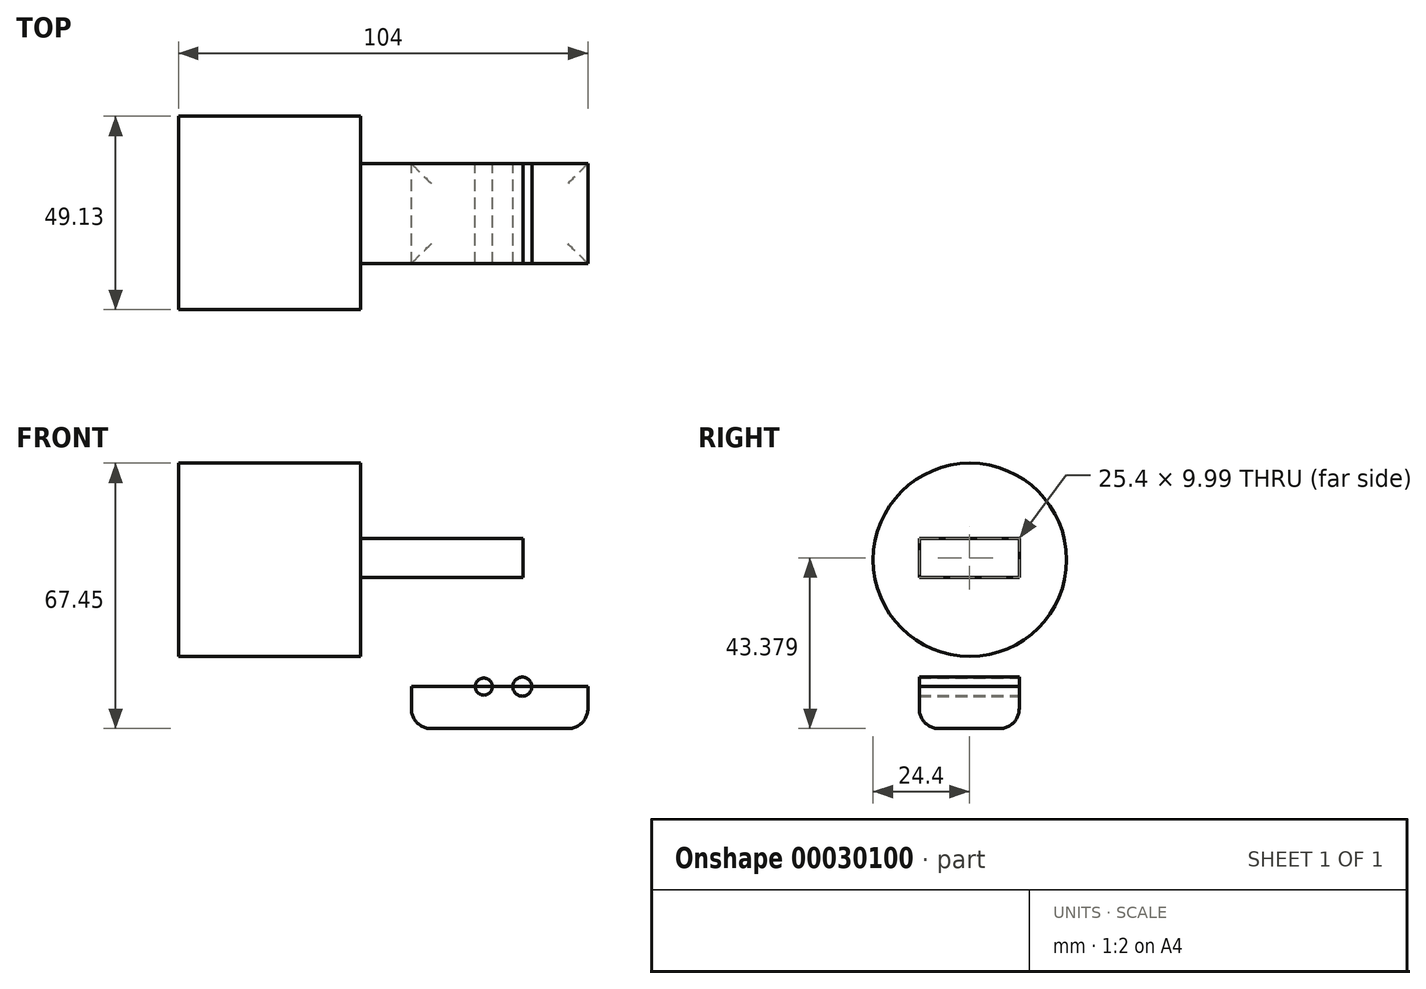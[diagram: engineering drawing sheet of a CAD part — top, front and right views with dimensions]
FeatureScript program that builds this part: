
annotation { "Feature Type Name" : "Feature", "Feature Type Description" : "" }
export const myFeature = defineFeature(function(context is Context, id is Id, definition is map)
    precondition{}
    {
        {
            var Q0;
            Q0=qCreatedBy(makeId("Front.planeOp"),FACE);
            var sketch = newSketch(context, id + "F0", { "sketchPlane" : qUnion([Q0])});
            skLineSegment(sketch, "E0.bottom", {"start": v(-46.22, 37.7) * mm, "end": v(41.33, 37.7) * mm});
            skLineSegment(sketch, "E0.top", {"start": v(-46.22, 27.71) * mm, "end": v(41.33, 27.71) * mm});
            skLineSegment(sketch, "E0.left", {"start": v(-46.22, 37.7) * mm, "end": v(-46.22, 27.71) * mm});
            skLineSegment(sketch, "E0.right", {"start": v(41.33, 37.7) * mm, "end": v(41.33, 27.71) * mm});
            skLineSegment(sketch, "E1.bottom", {"start": v(31.14, 27.71) * mm, "end": v(41.13, 27.71) * mm});
            skLineSegment(sketch, "E1.top", {"start": v(31.14, 0) * mm, "end": v(41.13, 0) * mm});
            skLineSegment(sketch, "E1.left", {"start": v(31.14, 27.71) * mm, "end": v(31.14, 0) * mm});
            skLineSegment(sketch, "E1.right", {"start": v(41.13, 27.71) * mm, "end": v(41.13, 0) * mm});
            skLineSegment(sketch, "E2.bottom", {"start": v(57.78, 0) * mm, "end": v(12.93, 0) * mm});
            skLineSegment(sketch, "E2.top", {"start": v(57.78, -10.67) * mm, "end": v(12.93, -10.67) * mm});
            skLineSegment(sketch, "E2.left", {"start": v(57.78, 0) * mm, "end": v(57.78, -10.67) * mm});
            skLineSegment(sketch, "E2.right", {"start": v(12.93, 0) * mm, "end": v(12.93, -10.67) * mm});
            skLineSegment(sketch, "E3.bottom", {"start": v(12.93, -10.67) * mm, "end": v(26.05, -10.67) * mm});
            skLineSegment(sketch, "E3.top", {"start": v(12.93, -35.94) * mm, "end": v(26.05, -35.94) * mm});
            skLineSegment(sketch, "E3.left", {"start": v(12.93, -10.67) * mm, "end": v(12.93, -35.94) * mm});
            skLineSegment(sketch, "E3.right", {"start": v(26.05, -10.67) * mm, "end": v(26.05, -35.94) * mm});
            skLineSegment(sketch, "E4.bottom", {"start": v(57.78, -10.67) * mm, "end": v(46.42, -10.67) * mm});
            skLineSegment(sketch, "E4.top", {"start": v(57.78, -36.72) * mm, "end": v(46.42, -36.72) * mm});
            skLineSegment(sketch, "E4.left", {"start": v(57.78, -10.67) * mm, "end": v(57.78, -36.72) * mm});
            skLineSegment(sketch, "E4.right", {"start": v(46.42, -10.67) * mm, "end": v(46.42, -36.72) * mm});
            skSolve(sketch);
        }
        {
            var Q0;
            Q0=qCreatedBy(makeId("Front.planeOp"),FACE);
            var sketch = newSketch(context, id + "F1", { "sketchPlane" : qUnion([Q0])});
            skCircle(sketch, "E5", {"center": v(31.34, 0) * mm, "radius": 2.17 * mm});
            skCircle(sketch, "E6", {"center": v(41.13, 0) * mm, "radius": 2.42 * mm});
            skSolve(sketch);
        }
        {
            var Q0;
            Q0=makeQuery(id+"F0.imprint","IMPRINT",FACE,{"disambiguationData":[TD([[makeQuery(id+"F0.imprint","IMPRINT",EDGE,{"derivedFrom":sQuery(id+"F0.wireOp",EDGE,"E0.bottom")}),-1.0]])]});
            var Q1;
            Q1=makeQuery(id+"F0.imprint","IMPRINT",FACE,{"disambiguationData":[TD([[makeQuery(id+"F0.imprint","IMPRINT",EDGE,{"derivedFrom":sQuery(id+"F0.wireOp",EDGE,"E1.bottom")}),-1.0]])]});
            var Q2;
            Q2=makeQuery(id+"F0.imprint","IMPRINT",FACE,{"disambiguationData":[TD([[makeQuery(id+"F0.imprint","IMPRINT",EDGE,{"derivedFrom":sQuery(id+"F0.wireOp",EDGE,"E2.top")}),-1.0]])]});
            var Q3;
            Q3=makeQuery(id+"F0.imprint","IMPRINT",FACE,{"disambiguationData":[TD([[makeQuery(id+"F0.imprint","IMPRINT",EDGE,{"derivedFrom":sQuery(id+"F0.wireOp",EDGE,"E3.bottom")}),-1.0]])]});
            var Q4;
            Q4=makeQuery(id+"F0.imprint","IMPRINT",FACE,{"disambiguationData":[TD([[makeQuery(id+"F0.imprint","IMPRINT",EDGE,{"derivedFrom":sQuery(id+"F0.wireOp",EDGE,"E4.bottom")}),1.0]])]});
            var Q5;
            Q5=makeQuery(id+"F1.imprint","IMPRINT",FACE,{"disambiguationData":[TD([[makeQuery(id+"F1.imprint","IMPRINT",EDGE,{"derivedFrom":sQuery(id+"F1.wireOp",EDGE,"E6")}),1.0]])]});
            var Q6;
            Q6=makeQuery(id+"F1.imprint","IMPRINT",FACE,{"disambiguationData":[TD([[makeQuery(id+"F1.imprint","IMPRINT",EDGE,{"derivedFrom":sQuery(id+"F1.wireOp",EDGE,"E5")}),1.0]])]});
            extrude(context, id + "F2", {"entities" : qUnion([Q0, Q1, Q2, Q3, Q4, Q5, Q6]), "depth" : 25.4 * mm});
        }
        {
            var Q0;
            Q0=makeQuery(id+"F2.opExtrude","SWEPT_FACE",FACE,{"disambiguationData":[OSD([sQuery(id+"F0.wireOp",EDGE,"E0.left")])]});
            var Q1;
            Q1=makeQuery(id+"F2.opExtrude","SWEPT_FACE",FACE,{"disambiguationData":[OSD([sQuery(id+"F0.wireOp",EDGE,"E0.bottom")])]});
            var Q2;
            Q2=makeQuery(id+"F2.opExtrude","CAP_FACE",FACE,{"disambiguationData":[OSD([sQuery(id+"F0.wireOp",EDGE,"E0.bottom"),sQuery(id+"F0.wireOp",EDGE,"E0.top"),sQuery(id+"F0.wireOp",EDGE,"E0.left"),sQuery(id+"F0.wireOp",EDGE,"E0.right"),sQuery(id+"F0.wireOp",EDGE,"E1.left"),sQuery(id+"F0.wireOp",EDGE,"E1.right"),sQuery(id+"F0.wireOp",EDGE,"E2.bottom"),sQuery(id+"F0.wireOp",EDGE,"E2.top"),sQuery(id+"F0.wireOp",EDGE,"E2.left"),sQuery(id+"F0.wireOp",EDGE,"E2.right"),sQuery(id+"F0.wireOp",EDGE,"E3.top"),sQuery(id+"F0.wireOp",EDGE,"E3.left"),sQuery(id+"F0.wireOp",EDGE,"E3.right"),sQuery(id+"F0.wireOp",EDGE,"E4.top"),sQuery(id+"F0.wireOp",EDGE,"E4.left"),sQuery(id+"F0.wireOp",EDGE,"E4.right")])],"isStart":false});
            var Q3;
            Q3=makeQuery(id+"F2.opExtrude","CAP_FACE",FACE,{"disambiguationData":[OSD([sQuery(id+"F0.wireOp",EDGE,"E0.bottom"),sQuery(id+"F0.wireOp",EDGE,"E0.top"),sQuery(id+"F0.wireOp",EDGE,"E0.left"),sQuery(id+"F0.wireOp",EDGE,"E0.right"),sQuery(id+"F0.wireOp",EDGE,"E1.left"),sQuery(id+"F0.wireOp",EDGE,"E1.right"),sQuery(id+"F0.wireOp",EDGE,"E2.bottom"),sQuery(id+"F0.wireOp",EDGE,"E2.top"),sQuery(id+"F0.wireOp",EDGE,"E2.left"),sQuery(id+"F0.wireOp",EDGE,"E2.right"),sQuery(id+"F0.wireOp",EDGE,"E3.top"),sQuery(id+"F0.wireOp",EDGE,"E3.left"),sQuery(id+"F0.wireOp",EDGE,"E3.right"),sQuery(id+"F0.wireOp",EDGE,"E4.top"),sQuery(id+"F0.wireOp",EDGE,"E4.left"),sQuery(id+"F0.wireOp",EDGE,"E4.right")])],"isStart":true});
            var Q4;
            Q4=makeQuery(id+"F2.opExtrude","SWEPT_FACE",FACE,{"disambiguationData":[OSD([sQuery(id+"F0.wireOp",EDGE,"E4.top")])]});
            var Q5;
            Q5=makeQuery(id+"F2.opExtrude","SWEPT_FACE",FACE,{"disambiguationData":[OSD([sQuery(id+"F0.wireOp",EDGE,"E2.top")])]});
            var Q6;
            Q6=makeQuery(id+"F2.opExtrude","SWEPT_FACE",FACE,{"disambiguationData":[OSD([sQuery(id+"F0.wireOp",EDGE,"E3.top")])]});
            fillet(context, id + "F3", {"entities" : qUnion([Q0, Q1, Q2, Q3, Q4, Q5, Q6]), "radius" : 5.08 * mm, "tangentPropagation" : true, "allowEdgeOverflow" : false});
        }
        {
            var Q0;
            Q0=qCreatedBy(makeId("Right.planeOp"),FACE);
            var sketch = newSketch(context, id + "F4", { "sketchPlane" : qUnion([Q0])});
            skCircle(sketch, "E7", {"center": v(-12.54, 32.22) * mm, "radius": 24.56 * mm});
            skSolve(sketch);
        }
        {
            var Q0;
            Q0 = qSketchRegion(id + "F4", true);
            extrude(context, id + "F5", {"entities" : qUnion([Q0]), "operationType" : NewBodyOperationType.ADD, "oppositeDirection" : true, "depth" : 46.18 * mm});
        }
    });
